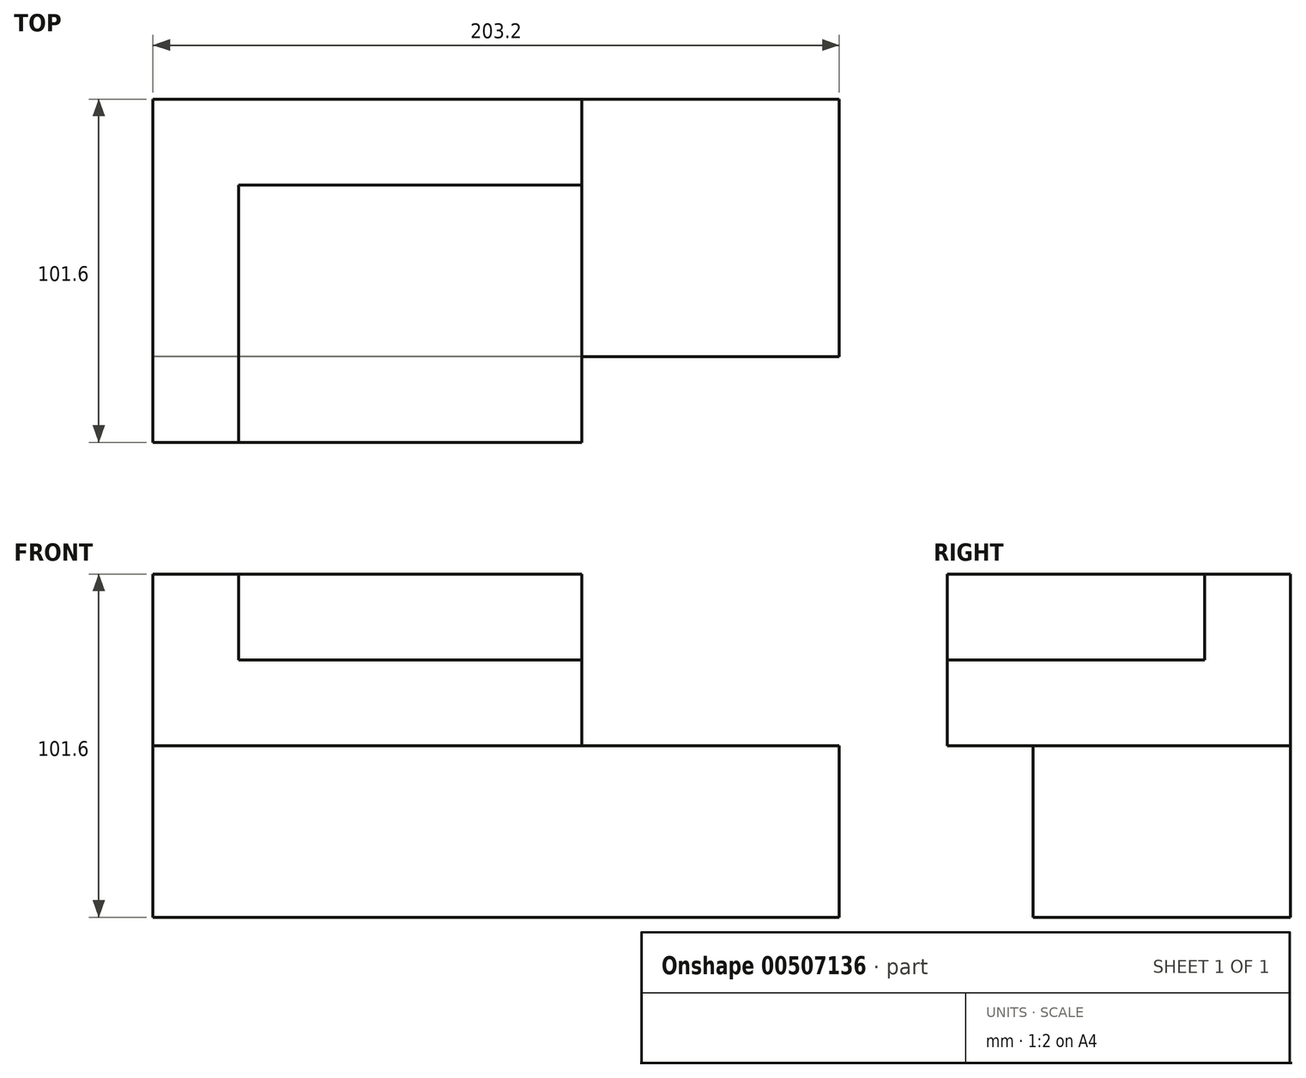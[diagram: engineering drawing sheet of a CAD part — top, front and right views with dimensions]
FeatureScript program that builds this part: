
annotation { "Feature Type Name" : "Feature", "Feature Type Description" : "" }
export const myFeature = defineFeature(function(context is Context, id is Id, definition is map)
    precondition{}
    {
        {
            var Q0;
            Q0=qCreatedBy(makeId("Front.planeOp"),FACE);
            var sketch = newSketch(context, id + "F0", { "sketchPlane" : qUnion([Q0])});
            skLineSegment(sketch, "E0.bottom", {"start": v(101.6, -70) * mm, "end": v(-101.6, -70) * mm});
            skLineSegment(sketch, "E0.top", {"start": v(101.6, -19.2) * mm, "end": v(-101.6, -19.2) * mm});
            skLineSegment(sketch, "E0.left", {"start": v(101.6, -70) * mm, "end": v(101.6, -19.2) * mm});
            skLineSegment(sketch, "E0.right", {"start": v(-101.6, -70) * mm, "end": v(-101.6, -19.2) * mm});
            skPoint(sketch, "E0.middle", {"position": v(0, -44.6) * mm});
            skSolve(sketch);
        }
        {
            var Q0;
            Q0=makeQuery(id+"F0.imprint","IMPRINT",FACE,{"disambiguationData":[TD([[makeQuery(id+"F0.imprint","IMPRINT",EDGE,{"derivedFrom":sQuery(id+"F0.wireOp",EDGE,"E0.bottom")}),-1.0]])]});
            extrude(context, id + "F1", {"entities" : qUnion([Q0]), "depth" : 76.2 * mm});
        }
        {
            var Q0;
            Q0=makeQuery(id+"F1.opExtrude","SWEPT_FACE",FACE,{"disambiguationData":[OSD([sQuery(id+"F0.wireOp",EDGE,"E0.top")])]});
            var sketch = newSketch(context, id + "F2", { "sketchPlane" : qUnion([Q0])});
            skLineSegment(sketch, "E1.bottom", {"start": v(-101.6, 0) * mm, "end": v(25.4, 0) * mm});
            skLineSegment(sketch, "E1.top", {"start": v(-101.6, -101.6) * mm, "end": v(25.4, -101.6) * mm});
            skLineSegment(sketch, "E1.left", {"start": v(-101.6, 0) * mm, "end": v(-101.6, -101.6) * mm});
            skLineSegment(sketch, "E1.right", {"start": v(25.4, 0) * mm, "end": v(25.4, -101.6) * mm});
            skLineSegment(sketch, "E2.bottom", {"start": v(25.4, -101.6) * mm, "end": v(-76.2, -101.6) * mm});
            skLineSegment(sketch, "E2.top", {"start": v(25.4, -25.4) * mm, "end": v(-76.2, -25.4) * mm});
            skLineSegment(sketch, "E2.left", {"start": v(25.4, -101.6) * mm, "end": v(25.4, -25.4) * mm});
            skLineSegment(sketch, "E2.right", {"start": v(-76.2, -101.6) * mm, "end": v(-76.2, -25.4) * mm});
            skSolve(sketch);
        }
        {
            var Q0;
            Q0 = qSketchRegion(id + "F2", true);
            extrude(context, id + "F3", {"entities" : qUnion([Q0]), "operationType" : NewBodyOperationType.ADD, "depth" : 50.8 * mm});
        }
        {
            var Q0;
            Q0=makeQuery(id+"F3.opExtrude","CAP_FACE",FACE,{"disambiguationData":[OSD([sQuery(id+"F2.wireOp",EDGE,"E1.bottom"),sQuery(id+"F2.wireOp",EDGE,"E1.top"),sQuery(id+"F2.wireOp",EDGE,"E1.left"),sQuery(id+"F2.wireOp",EDGE,"E1.right"),sQuery(id+"F2.wireOp",EDGE,"E2.bottom"),sQuery(id+"F2.wireOp",EDGE,"E2.left")])],"isStart":false});
            var sketch = newSketch(context, id + "F4", { "sketchPlane" : qUnion([Q0])});
            skLineSegment(sketch, "E3.bottom", {"start": v(-76.2, -25.4) * mm, "end": v(25.4, -25.4) * mm});
            skLineSegment(sketch, "E3.top", {"start": v(-76.2, -101.6) * mm, "end": v(25.4, -101.6) * mm});
            skLineSegment(sketch, "E3.left", {"start": v(-76.2, -25.4) * mm, "end": v(-76.2, -101.6) * mm});
            skLineSegment(sketch, "E3.right", {"start": v(25.4, -25.4) * mm, "end": v(25.4, -101.6) * mm});
            skSolve(sketch);
        }
        {
            var Q0;
            Q0=makeQuery(id+"F4.imprint","IMPRINT",FACE,{"disambiguationData":[TD([[makeQuery(id+"F4.imprint","IMPRINT",EDGE,{"derivedFrom":sQuery(id+"F4.wireOp",EDGE,"E3.bottom")}),-1.0]])]});
            extrude(context, id + "F5", {"entities" : qUnion([Q0]), "operationType" : NewBodyOperationType.REMOVE, "oppositeDirection" : true, "depth" : 25.4 * mm});
        }
    });
